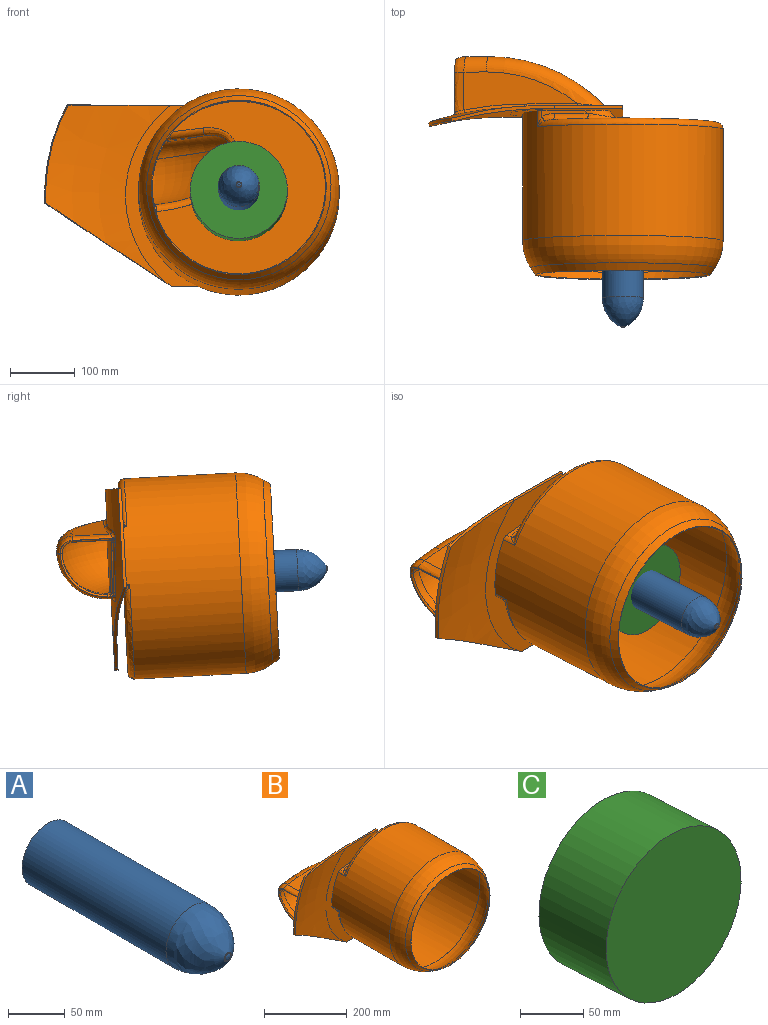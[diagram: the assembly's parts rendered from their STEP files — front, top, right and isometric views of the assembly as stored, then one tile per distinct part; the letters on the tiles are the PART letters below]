
ASSEMBLY  parts=3 mates=2
PART A: 6 faces, bbox 128.1x225.1x64.1 mm
  f0: plane 0.79x0.79mm, normal (0,-1,0), area 0.4mm2, adj f5
  f1: plane 64x64mm, normal (0,1,0), area 3217mm2, adj f2
  f2: cylinder r=32mm len=179.1mm, axis (0,-1,0), area 36009.9mm2, adj f1,f4
  f3: cone r=32mm half-angle=63.4deg, axis (0,1,0), area 24.3mm2, adj f4,f5
  f4: bspline ~128x64mm, area 7789.8mm2, adj f2,f3
  f5: bspline ~13.91x6.96mm, area 39.6mm2, adj f0,f3
PART B: 117 faces, bbox 531.5x364.8x484.3 mm
  f0: plane 3.54x1.11mm, normal (-0.99,0,-0.12), area 1.2mm2, adj f73,f92,f104
  f1: cylinder r=155mm len=310mm, axis (0,-1,0), area 170121.3mm2, adj f5,f6,f78,f84,f103
  f2: plane 175.28x58.62mm, normal (-0.12,0,0.99), area 6838.7mm2, adj f57,f67,f76,f115,f116
  f3: torus R=225mm, axis (-0.12,0,0.99), area 474.2mm2, adj f4,f72,f88,f103
  f4: torus R=175mm, axis (0.12,0,-0.99), area 1613.8mm2, adj f3,f58,f71,f103
  f5: cylinder r=10mm len=25mm, axis (0,-1,0), area 203mm2, adj f1,f58,f90,f103
  f6: cylinder r=10mm len=25mm, axis (0,-1,0), area 157.6mm2, adj f1,f69,f72,f103
  f7: bspline ~4.52x4.46mm, area 8.8mm2, adj f8,f11,f53,f89
  f8: bspline ~77.24x9.71mm, area 116.8mm2, adj f7,f9,f38,f75
  f9: bspline ~4.73x4.52mm, area 9.2mm2, adj f8,f11,f43,f82
  f10: cone r=135mm half-angle=56.3deg, axis (0,-1,0), area 1266.5mm2, adj f31,f68
  f11: plane 86.5x73.84mm, normal (0.99,0,0.12), area 288.1mm2, adj f7,f9,f27,f29,f41,f42,f64,f66
  f12: bspline ~77.28x10.67mm, area 144.1mm2, adj f13,f14,f38,f50
  f13: bspline ~6.39x6.24mm, area 18.2mm2, adj f12,f28,f43,f50,f55
  f14: bspline ~6.1x6.07mm, area 17.4mm2, adj f12,f15,f24,f50,f53
  f15: plane 5.87x4.31mm, normal (0.99,0,0.12), area 6.6mm2, adj f14,f36,f50
  f16: cylinder r=11.5mm len=16.83mm, axis (-0.99,0,-0.12), area 280.8mm2, adj f21,f34,f51,f54
  f17: cylinder r=153.5mm len=307mm, axis (0,-1,0), area 169073.6mm2, adj f18,f19,f40,f45,f48,f49
  f18: plane 104.65x51.14mm, normal (0,1,0), area 2270.5mm2, adj f17,f19,f22,f35,f46,f49,f50
  f19: bspline ~9.73x8.21mm, area 78.6mm2, adj f17,f18,f46,f48
  f20: bspline ~64.32x12.98mm, area 901.2mm2, adj f28,f33,f35,f50,f55
  f21: plane 15.43x6.02mm, normal (-0.12,0,0.99), area 49mm2, adj f16,f46,f48
  f22: plane 69.39x8.6mm, normal (-0.12,0,0.99), area 293.4mm2, adj f18,f36,f44,f46,f50
  f23: bspline ~70.01x69.67mm, area 255.8mm2, adj f24,f27,f37,f47
  f24: cylinder r=1.5mm len=4.45mm, axis (0,-1,0), area 10.5mm2, adj f14,f23,f36,f42
  f25: bspline ~19.07x13.76mm, area 252.1mm2, adj f26,f32,f35,f40
  f26: cylinder r=11.5mm len=53.67mm, axis (-0.99,0,-0.12), area 951.4mm2, adj f25,f35,f51,f52
  f27: bspline ~69.45x68.5mm, area 1291.2mm2, adj f11,f23,f41,f42
  f28: cylinder r=1.5mm len=57.51mm, axis (0,1,0), area 135.5mm2, adj f13,f20,f29,f47
  f29: plane 57.51x11.92mm, normal (-0.12,0,0.99), area 675.9mm2, adj f11,f28,f41,f43
  f30: cylinder r=23.5mm len=37.6mm, axis (0.99,0,0.12), area 1292mm2, adj f33,f35,f39,f44
  f31: cone r=153.75mm half-angle=33.7deg, axis (0,1,0), area 11527.4mm2, adj f10,f45
  f32: bspline ~15.03x10.87mm, area 61mm2, adj f25,f40,f49
  f33: bspline ~24.97x23.5mm, area 508.1mm2, adj f20,f30,f37,f47
  f34: bspline ~125.01x100.7mm, area 2284.3mm2, adj f16,f46,f51,f52
  f35: plane 191.78x70mm, normal (0.12,0,-0.99), area 8224.6mm2, adj f18,f20,f25,f26,f30,f39,f49,f50
  f36: bspline ~13.83x10.34mm, area 131.3mm2, adj f15,f22,f24,f37,f50
  f37: bspline ~73.5x73.28mm, area 1635.1mm2, adj f23,f33,f36,f44
  f38: bspline ~83.7x36.22mm, area 983.1mm2, adj f8,f12,f43,f53
  f39: torus R=225mm, axis (-0.12,0,0.99), area 7484.1mm2, adj f30,f35,f46,f52
  f40: torus R=145mm, axis (0,1,0), area 11088.8mm2, adj f17,f25,f32,f51,f54
  f41: bspline ~19.82x18.5mm, area 348.8mm2, adj f11,f27,f29,f47
  f42: plane 11.92x4.45mm, normal (0.12,0,-0.99), area 41.1mm2, adj f11,f24,f27,f53
  f43: bspline ~14.66x7.34mm, area 92.3mm2, adj f9,f13,f29,f38
  f44: cylinder r=73.5mm len=77.22mm, axis (0.99,0,0.12), area 4040.9mm2, adj f22,f30,f37,f46
  f45: torus R=80mm, axis (0,-1,0), area 40552.2mm2, adj f17,f31
  f46: torus R=175mm, axis (0.12,0,-0.99), area 20116mm2, adj f18,f19,f21,f22,f34,f39,f44
  f47: bspline ~20.01x19.85mm, area 70.5mm2, adj f23,f28,f33,f41
  f48: cylinder r=8.5mm len=26.02mm, axis (0,-1,0), area 186.6mm2, adj f17,f19,f21,f54
  f49: cylinder r=8.5mm len=31.5mm, axis (0,-1,0), area 183.7mm2, adj f17,f18,f32,f35
  f50: bspline ~154.57x115.71mm, area 8107.1mm2, adj f12,f13,f14,f15,f18,f20,f22,f35
  f51: plane 290.98x288.34mm, normal (0,-1,0), area 52197.6mm2, adj f16,f26,f34,f40,f52
  f52: bspline ~50.66x30.66mm, area 754.9mm2, adj f26,f34,f39,f51
  f53: bspline ~13.79x6.62mm, area 87.2mm2, adj f7,f14,f38,f42
  f54: bspline ~20x19.42mm, area 112.2mm2, adj f16,f40,f48
  f55: plane 6.46x4.93mm, normal (0.99,0,0.12), area 8.4mm2, adj f13,f20,f50
  f56: cylinder r=10mm len=16.65mm, axis (-0.99,0,-0.12), area 244.1mm2, adj f58,f71,f87,f90
  f57: bspline ~72.39x14.89mm, area 1006.5mm2, adj f2,f65,f70,f91,f113
  f58: plane 15.43x5mm, normal (0.12,0,-0.99), area 47.4mm2, adj f4,f5,f56,f103
  f59: plane 44.57x5.47mm, normal (0.12,0,-0.99), area 86.7mm2, adj f73,f83,f85,f108
  f60: bspline ~70.01x69.85mm, area 504.2mm2, adj f61,f64,f74,f86
  f61: cylinder r=3mm len=4.45mm, axis (0,-1,0), area 20.9mm2, adj f60,f73,f81,f92
  f62: bspline ~19.07x12.48mm, area 225.5mm2, adj f63,f69,f72,f78
  f63: cylinder r=10mm len=53.49mm, axis (-0.99,0,-0.12), area 827.3mm2, adj f62,f72,f87,f88
  f64: bspline ~67.96x67mm, area 1262.9mm2, adj f11,f60,f80,f81
  f65: cylinder r=3mm len=57.51mm, axis (0,1,0), area 271mm2, adj f57,f66,f79,f86
  f66: plane 57.51x11.92mm, normal (0.12,0,-0.99), area 675.9mm2, adj f11,f65,f80,f82
  f67: cylinder r=25mm len=37.79mm, axis (0.99,0,0.12), area 1374.4mm2, adj f2,f70,f76,f83
  f68: cone r=155mm half-angle=33.7deg, axis (0,1,0), area 11632.1mm2, adj f10,f84
  f69: bspline ~15.03x11.37mm, area 57.4mm2, adj f6,f62,f78
  f70: bspline ~26.64x25mm, area 621.4mm2, adj f57,f67,f74,f86
  f71: bspline ~124.82x100.7mm, area 1998.9mm2, adj f4,f56,f87,f88
  f72: plane 71.36x9.98mm, normal (-0.12,0,0.99), area 375.8mm2, adj f3,f6,f62,f63,f103
  f73: bspline ~15.5x13.29mm, area 101.3mm2, adj f0,f59,f61,f74,f106
  f74: bspline ~76.27x75mm, area 1933.4mm2, adj f60,f70,f73,f83
  f75: bspline ~83.8x36.34mm, area 987.9mm2, adj f8,f77,f82,f89
  f76: torus R=225mm, axis (-0.12,0,0.99), area 7079.2mm2, adj f2,f67,f85,f114
  f77: bspline ~77.51x11.76mm, area 247mm2, adj f75,f79,f92,f107
  f78: torus R=145mm, axis (0,1,0), area 13129.1mm2, adj f1,f62,f69,f87,f90
  f79: bspline ~6.39x6.24mm, area 27.7mm2, adj f65,f77,f82,f91,f109
  f80: bspline ~18.34x17mm, area 320.5mm2, adj f11,f64,f66,f86
  f81: plane 11.92x4.45mm, normal (-0.12,0,0.99), area 41.1mm2, adj f11,f61,f64,f89
  f82: bspline ~14.21x5.76mm, area 61.6mm2, adj f9,f66,f75,f79
  f83: cylinder r=75mm len=78.71mm, axis (0.99,0,0.12), area 4123.3mm2, adj f59,f67,f74,f85
  f84: torus R=80mm, axis (0,-1,0), area 41771.9mm2, adj f1,f68
  f85: torus R=175mm, axis (0.12,0,-0.99), area 17453.9mm2, adj f59,f76,f83,f110,f112
  f86: bspline ~20.19x19.85mm, area 133.9mm2, adj f60,f65,f70,f80
  f87: plane 290.98x288.34mm, normal (0,1,0), area 52197.6mm2, adj f56,f63,f71,f78,f88
  f88: bspline ~50.66x30.71mm, area 669.7mm2, adj f3,f63,f71,f87
  f89: bspline ~13.57x5.15mm, area 58.3mm2, adj f7,f75,f81,f92
  f90: bspline ~20x19.36mm, area 115.1mm2, adj f5,f56,f78
  f91: plane 4.3x1.59mm, normal (-0.99,0,-0.12), area 2.2mm2, adj f57,f79,f111
  f92: bspline ~6.23x6.1mm, area 26.2mm2, adj f0,f61,f77,f89,f105
  f93: bspline ~475.65x251.44mm, area 17379.2mm2, adj f94,f95,f100,f101,f104,f105,f106,f107
  f94: plane 280.04x173.16mm, normal (0,1,0), area 28995.3mm2, adj f93,f96,f97,f98,f99,f112,f114,f116
  f95: bspline ~188.58x122.89mm, area 1130.1mm2, adj f93,f96,f101,f102
  f96: plane 7.24x5mm, normal (-0.55,0,-0.84), area 43.2mm2, adj f94,f95,f97,f103
  f97: plane 103.93x5mm, normal (0,0,-1), area 519.6mm2, adj f94,f96,f98,f103
  f98: plane 280x5mm, normal (1,0,0), area 1400mm2, adj f94,f97,f99,f103
  f99: plane 105.17x5mm, normal (0,0,1), area 525.8mm2, adj f94,f98,f100,f103
  f100: bspline ~160.16x24.75mm, area 806.3mm2, adj f93,f99,f101,f102
  f101: cone r=300mm half-angle=18.2deg, axis (0,1,0), area 788.5mm2, adj f93,f95,f100,f102
  f102: bspline ~469.19x191.24mm, area 33729.9mm2, adj f95,f100,f101,f103
  f103: plane 288.67x183.77mm, normal (0,-1,0), area 31929.3mm2, adj f1,f3,f4,f5,f6,f58,f72,f96
  f104: bspline ~4.91x4.12mm, area 7.6mm2, adj f0,f93,f105,f106
  f105: bspline ~5.35x4.9mm, area 28.3mm2, adj f92,f93,f104,f107
  f106: bspline ~20.82x8.41mm, area 149.6mm2, adj f73,f93,f104,f108
  f107: bspline ~77.57x13.09mm, area 403.1mm2, adj f77,f93,f105,f109
  f108: bspline ~45.36x10.33mm, area 351.1mm2, adj f59,f93,f106,f110
  f109: bspline ~5.45x4.86mm, area 27mm2, adj f79,f93,f107,f111
  f110: bspline ~15.56x6.79mm, area 116.6mm2, adj f85,f93,f108,f112
  f111: bspline ~4.99x4.03mm, area 10.7mm2, adj f91,f93,f109,f113
  f112: bspline ~150.75x98.94mm, area 1141mm2, adj f85,f94,f110,f114
  f113: bspline ~19.05x12.34mm, area 142.5mm2, adj f57,f93,f111,f115
  f114: bspline ~47.38x25.58mm, area 312.9mm2, adj f76,f94,f112,f116
  f115: bspline ~94.17x16.53mm, area 722.8mm2, adj f2,f93,f113,f116
  f116: cylinder r=5mm len=81.55mm, axis (0.99,0,0.12), area 640.5mm2, adj f2,f94,f114,f115
PART C: 3 faces, bbox 150x82.7x153.7 mm
  f0: plane 150x149.79mm, normal (0,-1,0.05), area 17671.5mm2, adj f1
  f1: cylinder r=75mm len=153.72mm, axis (0,-1,0.05), area 35342.9mm2, adj f0,f2
  f2: plane 150x149.79mm, normal (0,1,-0.05), area 17671.5mm2, adj f1
PLACE A rot(axis=(-1,0,0),3deg) t=(0,-656.04,288.42)mm
PLACE B rot(axis=(-1,0,0),3deg) t=(0,-565.17,283.66)mm
PLACE C at identity fixed
MATE fastened A.f2 <-> C.f1  axis (0,-1,0.05) through (0,-656.04,288.42)mm
MATE fastened B.f1 <-> C.f1  axis (0,1,-0.05) through (0,-565.17,283.66)mm
